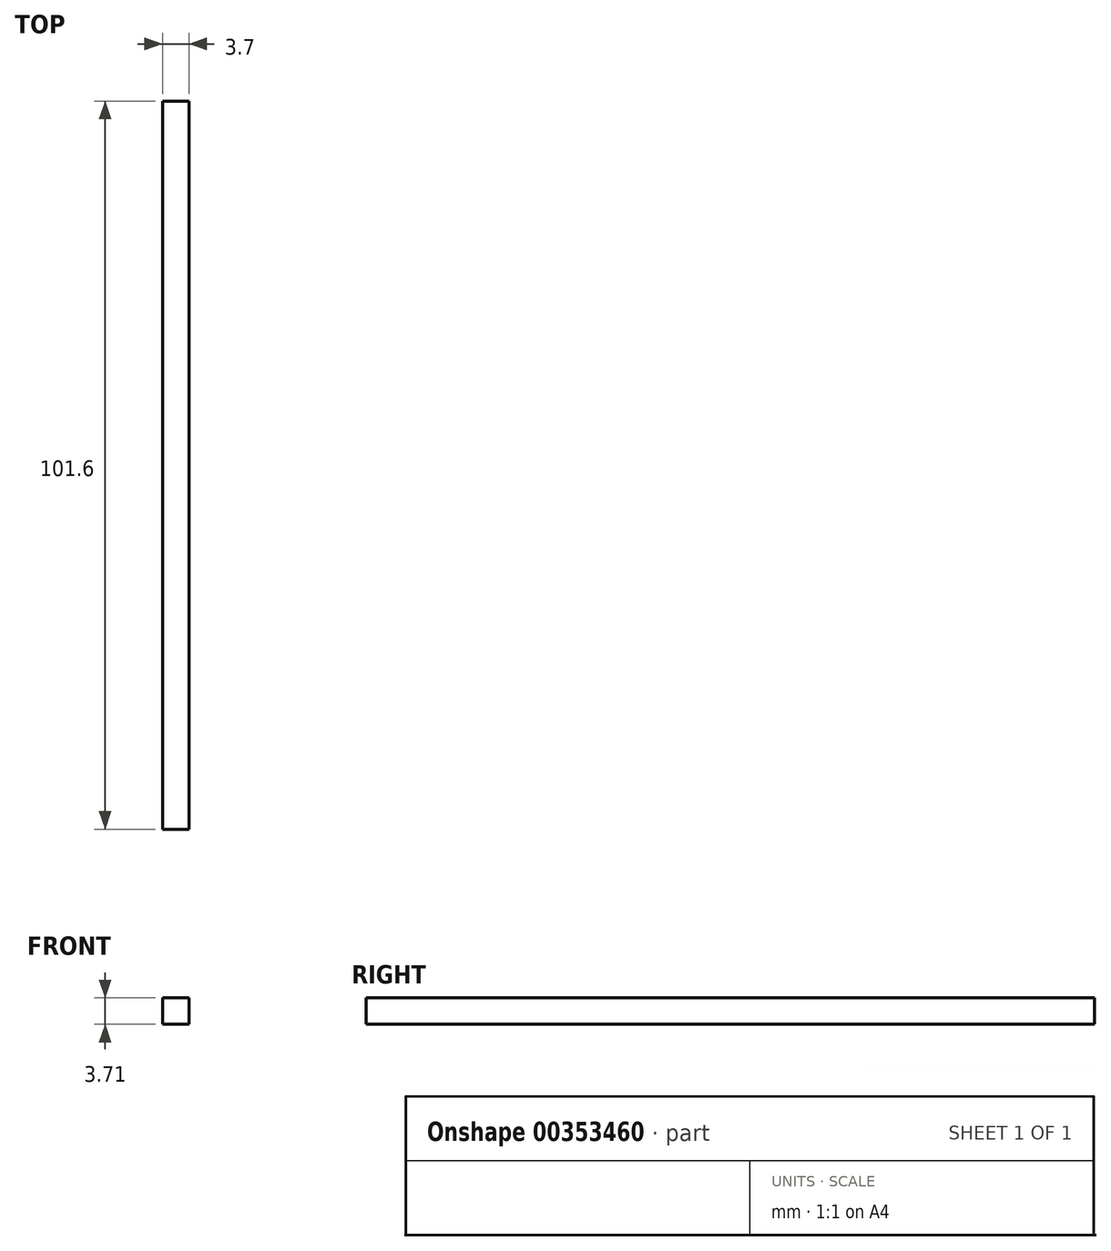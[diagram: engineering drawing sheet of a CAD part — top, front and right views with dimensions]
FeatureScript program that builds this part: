
annotation { "Feature Type Name" : "Feature", "Feature Type Description" : "" }
export const myFeature = defineFeature(function(context is Context, id is Id, definition is map)
    precondition{}
    {
        {
            var Q0;
            Q0=qCreatedBy(makeId("Front.planeOp"),FACE);
            var sketch = newSketch(context, id + "F0", { "sketchPlane" : qUnion([Q0])});
            skLineSegment(sketch, "E0.bottom", {"start": v(-58.47, 58.05) * mm, "end": v(-54.77, 58.05) * mm});
            skLineSegment(sketch, "E0.top", {"start": v(-58.47, 54.34) * mm, "end": v(-54.77, 54.34) * mm});
            skLineSegment(sketch, "E0.left", {"start": v(-58.47, 58.05) * mm, "end": v(-58.47, 54.34) * mm});
            skLineSegment(sketch, "E0.right", {"start": v(-54.77, 58.05) * mm, "end": v(-54.77, 54.34) * mm});
            skSolve(sketch);
        }
        {
            var Q0;
            Q0 = qSketchRegion(id + "F0", true);
            extrude(context, id + "F1", {"entities" : qUnion([Q0]), "depth" : 101.6 * mm});
        }
    });
